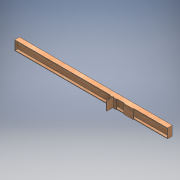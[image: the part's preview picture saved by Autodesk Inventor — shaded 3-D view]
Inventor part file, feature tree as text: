
AUTODESK INVENTOR PART (.ipt)
format: ipt  version: 2016 (Build 200138000, 138)  size: 174,080 bytes
history: native  units: mm
features: extrude x4, sketch x4
ambient origin geometry x8: Origin, YZ Plane, XZ Plane, XY Plane, X Axis, Y Axis, Z Axis, Center Point
bodies: Solid1 (feature_tree)
feature tree (8):
  extrude  "Extrusion1"  Depth=50.0mm
  extrude  "Extrusion2"  Depth=803.0mm
  extrude  "Extrusion3"  Depth=3.0mm
  extrude  "Extrusion4"  Depth=3.0mm
  sketch  "Sketch1"  dims[d0=809.0mm d1=50.0mm]
  sketch  "Sketch2"  dims[d2=3.0mm d3=0.0mm d4=803.0mm]
  sketch  "Sketch3"  dims[d5=44.0mm d6=3.0mm]
  sketch  "Sketch4"  dims[d7=3.0mm d8=3.0mm d9=600.0mm d10=12.5mm d11=12.5mm d12=0.0mm d13=0.0mm d14=50.0mm d15=23.5mm d16=3.0mm d17=0.0mm d18=15.0mm d19=40.0mm d20=3.0mm d21=44.0mm d22=50.0mm d23=0.0mm d24=3.0mm d25=15.0mm d26=50.0mm]
